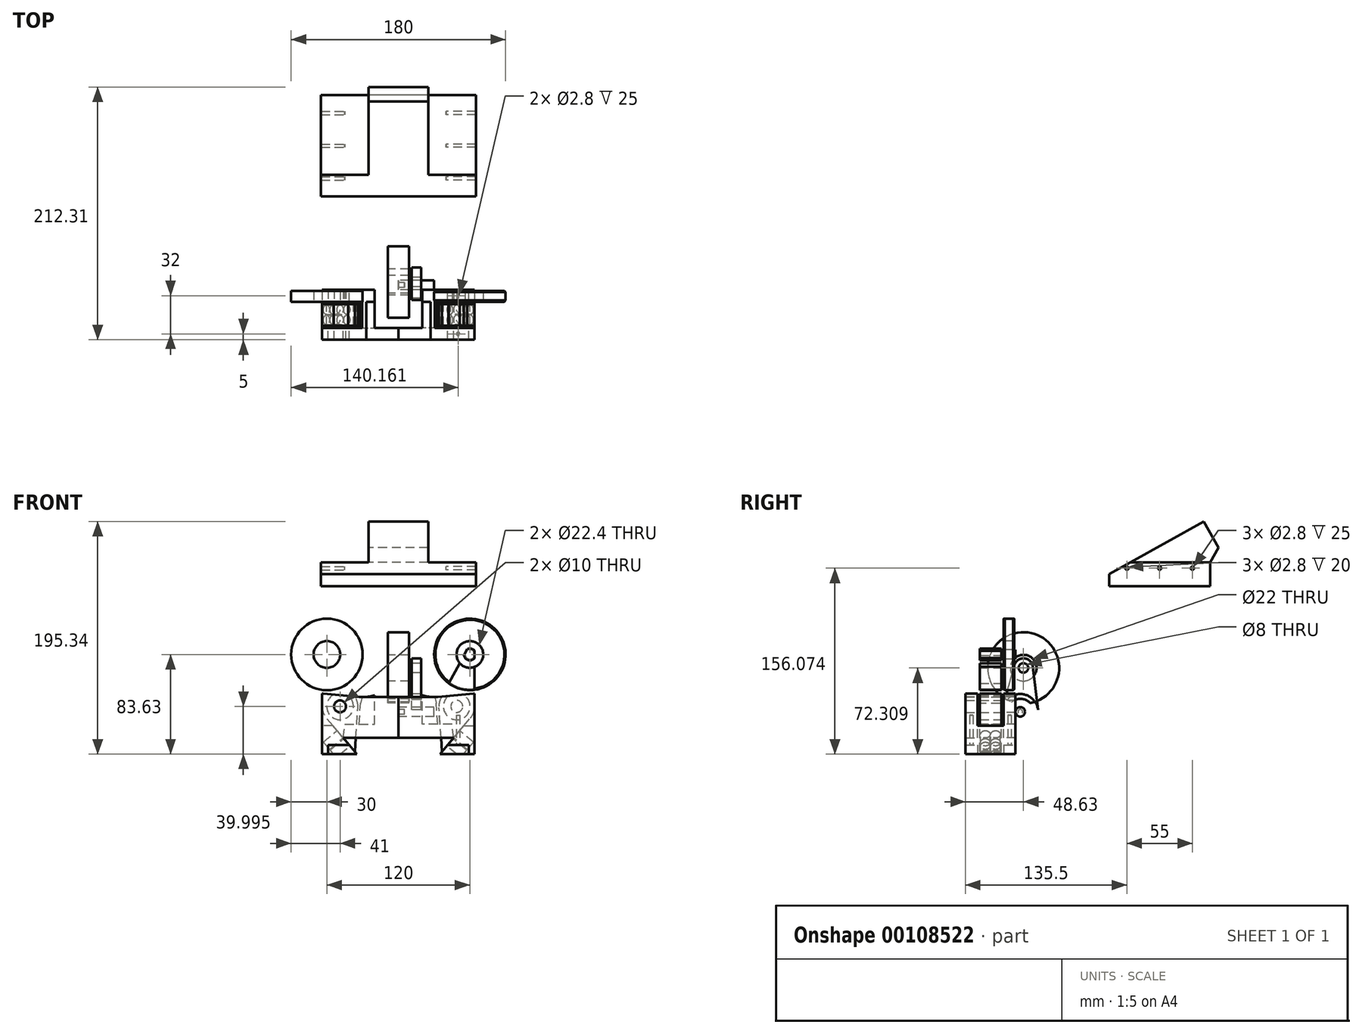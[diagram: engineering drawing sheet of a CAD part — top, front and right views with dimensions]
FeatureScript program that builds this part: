
annotation { "Feature Type Name" : "Feature", "Feature Type Description" : "" }
export const myFeature = defineFeature(function(context is Context, id is Id, definition is map)
    precondition{}
    {
        {
            var Q0;
            Q0=qCreatedBy(makeId("Right.planeOp"),FACE);
            var sketch = newSketch(context, id + "F0", { "sketchPlane" : qUnion([Q0])});
            skLineSegment(sketch, "E0", {"start": v(0, 0) * mm, "end": v(214.16, 119) * mm, "construction": true});
            skPoint(sketch, "E1", {"position": v(196.68, 109.28) * mm});
            skPoint(sketch, "E2", {"position": v(103.39, 57.44) * mm});
            skLineSegment(sketch, "E3", {"start": v(172.6, 107.34) * mm, "end": v(182.3, 89.85) * mm});
            skPoint(sketch, "E4", {"position": v(164.34, 91.3) * mm});
            skLineSegment(sketch, "E5", {"start": v(172.6, 107.34) * mm, "end": v(170.16, 111.7) * mm});
            skLineSegment(sketch, "E6", {"start": v(170.16, 111.7) * mm, "end": v(90.5, 67.44) * mm});
            skLineSegment(sketch, "E7", {"start": v(175.5, 77.44) * mm, "end": v(90.5, 77.44) * mm});
            skLineSegment(sketch, "E8", {"start": v(90.5, 77.44) * mm, "end": v(90.5, 67.44) * mm});
            skLineSegment(sketch, "E9", {"start": v(175.5, 77.44) * mm, "end": v(175.5, 57.44) * mm});
            skLineSegment(sketch, "E10", {"start": v(175.5, 57.44) * mm, "end": v(90.5, 57.44) * mm});
            skLineSegment(sketch, "E11", {"start": v(90.5, 57.44) * mm, "end": v(90.5, 67.44) * mm});
            skLineSegment(sketch, "E12", {"start": v(182.3, 89.85) * mm, "end": v(175.5, 77.44) * mm});
            skSolve(sketch);
        }
        {
            var Q0;
            Q0=qCreatedBy(makeId("Right.planeOp"),FACE);
            var sketch = newSketch(context, id + "F1", { "sketchPlane" : qUnion([Q0])});
            skLineSegment(sketch, "E13", {"start": v(160.5, 72.44) * mm, "end": v(105.5, 72.44) * mm, "construction": true});
            skPoint(sketch, "E14", {"position": v(133, 72.44) * mm});
            skCircle(sketch, "E15", {"center": v(160.5, 72.44) * mm, "radius": 1.4 * mm});
            skCircle(sketch, "E16", {"center": v(133, 72.44) * mm, "radius": 1.4 * mm});
            skCircle(sketch, "E17", {"center": v(105.5, 72.44) * mm, "radius": 1.4 * mm});
            skSolve(sketch);
        }
        {
            var Q0;
            {var subQ0=sQuery(id+"F0.wireOp",EDGE,"E5");Q0=makeQuery(id+"F0.imprint","IMPRINT",FACE,{"disambiguationData":[TD([[makeQuery(id+"F0.imprint","IMPRINT",EDGE,{"derivedFrom":subQ0}),1.0]])]});}
            var Q1;
            {var subQ0=sQuery(id+"F0.wireOp",EDGE,"E9");Q1=makeQuery(id+"F0.imprint","IMPRINT",FACE,{"disambiguationData":[TD([[makeQuery(id+"F0.imprint","IMPRINT",EDGE,{"derivedFrom":subQ0}),-1.0]])]});}
            var Q2;
            {var subQ0=sQuery(id+"F0.wireOp",EDGE,"E12");Q2=makeQuery(id+"F0.imprint","IMPRINT",FACE,{"disambiguationData":[TD([[makeQuery(id+"F0.imprint","IMPRINT",EDGE,{"derivedFrom":subQ0}),-1.0]])]});}
            var Q3;
            {var subQ8=sQuery(id+"F0.wireOp",EDGE,"E11");Q3=makeQuery(id+"F0.imprint","IMPRINT",FACE,{"disambiguationData":[TD([[makeQuery(id+"F0.imprint","IMPRINT",EDGE,{"derivedFrom":subQ8}),-1.0]])]});}
            var Q4;
            {var subQ0=sQuery(id+"F0.wireOp",EDGE,"E10");var subQ1=sQuery(id+"F0.wireOp",EDGE,"sEXiXuxS-OCvZ-XF6I-7GhH-brnsfU8Oz83V");var subQ2=makeQuery(id+"F0.imprint","INTERSECT",VERTEX,{"derivedFrom":[subQ1,subQ0]});Q4=makeQuery(id+"F0.imprint","IMPRINT",FACE,{"disambiguationData":[TD([[makeQuery(id+"F0.imprint","IMPRINT",EDGE,{"disambiguationData":[TD([[subQ2,1.0]])],"derivedFrom":subQ1}),1.0]])]});}
            extrude(context, id + "F2", {"entities" : qUnion([Q0, Q1, Q2, Q3, Q4]), "endBound" : BoundingType.SYMMETRIC, "depth" : 50 * mm});
        }
        {
            var Q0;
            {var subQ0=sQuery(id+"F0.wireOp",EDGE,"E9");Q0=makeQuery(id+"F0.imprint","IMPRINT",FACE,{"disambiguationData":[TD([[makeQuery(id+"F0.imprint","IMPRINT",EDGE,{"derivedFrom":subQ0}),-1.0]])]});}
            var Q1;
            {var subQ0=sQuery(id+"F0.wireOp",EDGE,"OFBeSH8e-VfH7-OQUe-lzTa-2fPhxgrnsW6p");var subQ1=sQuery(id+"F0.wireOp",EDGE,"9e1fb45d-ffff-4d52-95ad-2ab2a11606bd.trimOffspring");var subQ2=makeQuery(id+"F0.imprint","INTERSECT",VERTEX,{"derivedFrom":[subQ1,subQ0]});Q1=makeQuery(id+"F0.imprint","IMPRINT",FACE,{"disambiguationData":[TD([[makeQuery(id+"F0.imprint","IMPRINT",EDGE,{"disambiguationData":[TD([[subQ2,1.0]])],"derivedFrom":subQ1}),-1.0]])]});}
            var Q2;
            {var subQ0=sQuery(id+"F0.wireOp",EDGE,"L8JwAmDp-Vegf-fPRI-g6yE-gIPxQeSgqsUd");var subQ1=sQuery(id+"F0.wireOp",EDGE,"OFBeSH8e-VfH7-OQUe-lzTa-2fPhxgrnsW6p");var subQ2=makeQuery(id+"F0.imprint","INTERSECT",VERTEX,{"derivedFrom":[subQ1,subQ0]});Q2=makeQuery(id+"F0.imprint","IMPRINT",FACE,{"disambiguationData":[TD([[makeQuery(id+"F0.imprint","IMPRINT",EDGE,{"disambiguationData":[TD([[subQ2,-1.0]])],"derivedFrom":subQ1}),-1.0]])]});}
            var Q3;
            {var subQ0=sQuery(id+"F0.wireOp",EDGE,"sEXiXuxS-OCvZ-XF6I-7GhH-brnsfU8Oz83V");var subQ1=sQuery(id+"F0.wireOp",EDGE,"OFBeSH8e-VfH7-OQUe-lzTa-2fPhxgrnsW6p");var subQ2=makeQuery(id+"F0.imprint","INTERSECT",VERTEX,{"derivedFrom":[subQ1,subQ0]});Q3=makeQuery(id+"F0.imprint","IMPRINT",FACE,{"disambiguationData":[TD([[makeQuery(id+"F0.imprint","IMPRINT",EDGE,{"disambiguationData":[TD([[subQ2,-1.0]])],"derivedFrom":subQ1}),-1.0]])]});}
            var Q4;
            {var subQ5=sQuery(id+"F0.wireOp",EDGE,"sEXiXuxS-OCvZ-XF6I-7GhH-brnsfU8Oz83V");var subQ6=sQuery(id+"F0.wireOp",EDGE,"l3UI67aI-0oty-dVZL-KV3C-MkyXoSJzeSSp");var subQ10=makeQuery(id+"F0.imprint","INTERSECT",VERTEX,{"disambiguationData":[OD(0.0)],"derivedFrom":[subQ6,subQ5]});Q4=makeQuery(id+"F0.imprint","IMPRINT",FACE,{"disambiguationData":[TD([[makeQuery(id+"F0.imprint","IMPRINT",EDGE,{"disambiguationData":[TD([[subQ10,1.0]])],"derivedFrom":subQ6}),-1.0]])]});}
            var Q5;
            {var subQ0=sQuery(id+"F0.wireOp",EDGE,"L8JwAmDp-Vegf-fPRI-g6yE-gIPxQeSgqsUd");var subQ1=sQuery(id+"F0.wireOp",EDGE,"l3UI67aI-0oty-dVZL-KV3C-MkyXoSJzeSSp");var subQ9=makeQuery(id+"F0.imprint","INTERSECT",VERTEX,{"disambiguationData":[OD(0.0)],"derivedFrom":[subQ1,subQ0]});Q5=makeQuery(id+"F0.imprint","IMPRINT",FACE,{"disambiguationData":[TD([[makeQuery(id+"F0.imprint","IMPRINT",EDGE,{"disambiguationData":[TD([[subQ9,-1.0]])],"derivedFrom":subQ1}),-1.0]])]});}
            var Q6;
            {var subQ0=sQuery(id+"F0.wireOp",EDGE,"sEXiXuxS-OCvZ-XF6I-7GhH-brnsfU8Oz83V");var subQ1=sQuery(id+"F0.wireOp",EDGE,"l3UI67aI-0oty-dVZL-KV3C-MkyXoSJzeSSp");var subQ2=makeQuery(id+"F0.imprint","INTERSECT",VERTEX,{"disambiguationData":[OD(1.0)],"derivedFrom":[subQ1,subQ0]});Q6=makeQuery(id+"F0.imprint","IMPRINT",FACE,{"disambiguationData":[TD([[makeQuery(id+"F0.imprint","IMPRINT",EDGE,{"disambiguationData":[TD([[subQ2,1.0]])],"derivedFrom":subQ1}),-1.0]])]});}
            var Q7;
            {var subQ0=sQuery(id+"F0.wireOp",EDGE,"sEXiXuxS-OCvZ-XF6I-7GhH-brnsfU8Oz83V");var subQ1=sQuery(id+"F0.wireOp",EDGE,"l3UI67aI-0oty-dVZL-KV3C-MkyXoSJzeSSp");var subQ2=makeQuery(id+"F0.imprint","INTERSECT",VERTEX,{"disambiguationData":[OD(0.0)],"derivedFrom":[subQ1,subQ0]});Q7=makeQuery(id+"F0.imprint","IMPRINT",FACE,{"disambiguationData":[TD([[makeQuery(id+"F0.imprint","IMPRINT",EDGE,{"disambiguationData":[TD([[subQ2,-1.0]])],"derivedFrom":subQ1}),-1.0]])]});}
            var Q8;
            {var subQ0=sQuery(id+"F0.wireOp",EDGE,"E10");var subQ1=sQuery(id+"F0.wireOp",EDGE,"sEXiXuxS-OCvZ-XF6I-7GhH-brnsfU8Oz83V");var subQ2=makeQuery(id+"F0.imprint","INTERSECT",VERTEX,{"derivedFrom":[subQ1,subQ0]});Q8=makeQuery(id+"F0.imprint","IMPRINT",FACE,{"disambiguationData":[TD([[makeQuery(id+"F0.imprint","IMPRINT",EDGE,{"disambiguationData":[TD([[subQ2,1.0]])],"derivedFrom":subQ1}),1.0]])]});}
            var Q9;
            {var subQ8=sQuery(id+"F0.wireOp",EDGE,"E11");Q9=makeQuery(id+"F0.imprint","IMPRINT",FACE,{"disambiguationData":[TD([[makeQuery(id+"F0.imprint","IMPRINT",EDGE,{"derivedFrom":subQ8}),-1.0]])]});}
            extrude(context, id + "F3", {"entities" : qUnion([Q0, Q1, Q2, Q3, Q4, Q5, Q6, Q7, Q8, Q9]), "operationType" : NewBodyOperationType.ADD, "oppositeDirection" : true, "depth" : 65 * mm, "hasSecondDirection" : true, "secondDirectionOppositeDirection" : true, "secondDirectionDepth" : 25 * mm});
        }
        {
            var Q0;
            {var subQ8=sQuery(id+"F0.wireOp",EDGE,"E11");Q0=makeQuery(id+"F0.imprint","IMPRINT",FACE,{"disambiguationData":[TD([[makeQuery(id+"F0.imprint","IMPRINT",EDGE,{"derivedFrom":subQ8}),-1.0]])]});}
            var Q1;
            {var subQ0=sQuery(id+"F0.wireOp",EDGE,"E10");var subQ1=sQuery(id+"F0.wireOp",EDGE,"sEXiXuxS-OCvZ-XF6I-7GhH-brnsfU8Oz83V");var subQ2=makeQuery(id+"F0.imprint","INTERSECT",VERTEX,{"derivedFrom":[subQ1,subQ0]});Q1=makeQuery(id+"F0.imprint","IMPRINT",FACE,{"disambiguationData":[TD([[makeQuery(id+"F0.imprint","IMPRINT",EDGE,{"disambiguationData":[TD([[subQ2,1.0]])],"derivedFrom":subQ1}),1.0]])]});}
            var Q2;
            {var subQ0=sQuery(id+"F0.wireOp",EDGE,"E9");Q2=makeQuery(id+"F0.imprint","IMPRINT",FACE,{"disambiguationData":[TD([[makeQuery(id+"F0.imprint","IMPRINT",EDGE,{"derivedFrom":subQ0}),-1.0]])]});}
            var Q3;
            {var subQ5=sQuery(id+"F0.wireOp",EDGE,"sEXiXuxS-OCvZ-XF6I-7GhH-brnsfU8Oz83V");var subQ6=sQuery(id+"F0.wireOp",EDGE,"l3UI67aI-0oty-dVZL-KV3C-MkyXoSJzeSSp");var subQ10=makeQuery(id+"F0.imprint","INTERSECT",VERTEX,{"disambiguationData":[OD(0.0)],"derivedFrom":[subQ6,subQ5]});Q3=makeQuery(id+"F0.imprint","IMPRINT",FACE,{"disambiguationData":[TD([[makeQuery(id+"F0.imprint","IMPRINT",EDGE,{"disambiguationData":[TD([[subQ10,1.0]])],"derivedFrom":subQ6}),-1.0]])]});}
            var Q4;
            {var subQ0=sQuery(id+"F0.wireOp",EDGE,"L8JwAmDp-Vegf-fPRI-g6yE-gIPxQeSgqsUd");var subQ1=sQuery(id+"F0.wireOp",EDGE,"l3UI67aI-0oty-dVZL-KV3C-MkyXoSJzeSSp");var subQ9=makeQuery(id+"F0.imprint","INTERSECT",VERTEX,{"disambiguationData":[OD(0.0)],"derivedFrom":[subQ1,subQ0]});Q4=makeQuery(id+"F0.imprint","IMPRINT",FACE,{"disambiguationData":[TD([[makeQuery(id+"F0.imprint","IMPRINT",EDGE,{"disambiguationData":[TD([[subQ9,-1.0]])],"derivedFrom":subQ1}),-1.0]])]});}
            var Q5;
            {var subQ0=sQuery(id+"F0.wireOp",EDGE,"sEXiXuxS-OCvZ-XF6I-7GhH-brnsfU8Oz83V");var subQ1=sQuery(id+"F0.wireOp",EDGE,"l3UI67aI-0oty-dVZL-KV3C-MkyXoSJzeSSp");var subQ2=makeQuery(id+"F0.imprint","INTERSECT",VERTEX,{"disambiguationData":[OD(1.0)],"derivedFrom":[subQ1,subQ0]});Q5=makeQuery(id+"F0.imprint","IMPRINT",FACE,{"disambiguationData":[TD([[makeQuery(id+"F0.imprint","IMPRINT",EDGE,{"disambiguationData":[TD([[subQ2,1.0]])],"derivedFrom":subQ1}),-1.0]])]});}
            var Q6;
            {var subQ0=sQuery(id+"F0.wireOp",EDGE,"OFBeSH8e-VfH7-OQUe-lzTa-2fPhxgrnsW6p");var subQ1=sQuery(id+"F0.wireOp",EDGE,"9e1fb45d-ffff-4d52-95ad-2ab2a11606bd.trimOffspring");var subQ2=makeQuery(id+"F0.imprint","INTERSECT",VERTEX,{"derivedFrom":[subQ1,subQ0]});Q6=makeQuery(id+"F0.imprint","IMPRINT",FACE,{"disambiguationData":[TD([[makeQuery(id+"F0.imprint","IMPRINT",EDGE,{"disambiguationData":[TD([[subQ2,1.0]])],"derivedFrom":subQ1}),-1.0]])]});}
            var Q7;
            {var subQ0=sQuery(id+"F0.wireOp",EDGE,"L8JwAmDp-Vegf-fPRI-g6yE-gIPxQeSgqsUd");var subQ1=sQuery(id+"F0.wireOp",EDGE,"OFBeSH8e-VfH7-OQUe-lzTa-2fPhxgrnsW6p");var subQ2=makeQuery(id+"F0.imprint","INTERSECT",VERTEX,{"derivedFrom":[subQ1,subQ0]});Q7=makeQuery(id+"F0.imprint","IMPRINT",FACE,{"disambiguationData":[TD([[makeQuery(id+"F0.imprint","IMPRINT",EDGE,{"disambiguationData":[TD([[subQ2,-1.0]])],"derivedFrom":subQ1}),-1.0]])]});}
            var Q8;
            {var subQ0=sQuery(id+"F0.wireOp",EDGE,"sEXiXuxS-OCvZ-XF6I-7GhH-brnsfU8Oz83V");var subQ1=sQuery(id+"F0.wireOp",EDGE,"OFBeSH8e-VfH7-OQUe-lzTa-2fPhxgrnsW6p");var subQ2=makeQuery(id+"F0.imprint","INTERSECT",VERTEX,{"derivedFrom":[subQ1,subQ0]});Q8=makeQuery(id+"F0.imprint","IMPRINT",FACE,{"disambiguationData":[TD([[makeQuery(id+"F0.imprint","IMPRINT",EDGE,{"disambiguationData":[TD([[subQ2,-1.0]])],"derivedFrom":subQ1}),-1.0]])]});}
            var Q9;
            {var subQ0=sQuery(id+"F0.wireOp",EDGE,"sEXiXuxS-OCvZ-XF6I-7GhH-brnsfU8Oz83V");var subQ1=sQuery(id+"F0.wireOp",EDGE,"l3UI67aI-0oty-dVZL-KV3C-MkyXoSJzeSSp");var subQ2=makeQuery(id+"F0.imprint","INTERSECT",VERTEX,{"disambiguationData":[OD(0.0)],"derivedFrom":[subQ1,subQ0]});Q9=makeQuery(id+"F0.imprint","IMPRINT",FACE,{"disambiguationData":[TD([[makeQuery(id+"F0.imprint","IMPRINT",EDGE,{"disambiguationData":[TD([[subQ2,-1.0]])],"derivedFrom":subQ1}),-1.0]])]});}
            extrude(context, id + "F4", {"entities" : qUnion([Q0, Q1, Q2, Q3, Q4, Q5, Q6, Q7, Q8, Q9]), "operationType" : NewBodyOperationType.ADD, "depth" : 65 * mm, "hasSecondDirection" : true, "secondDirectionOppositeDirection" : false, "secondDirectionDepth" : 25 * mm});
        }
        {
            var Q0;
            Q0=makeQuery(id+"F1.imprint","IMPRINT",FACE,{"disambiguationData":[TD([[makeQuery(id+"F1.imprint","IMPRINT",EDGE,{"derivedFrom":sQuery(id+"F1.wireOp",EDGE,"E17")}),1.0]])]});
            var Q1;
            Q1=makeQuery(id+"F1.imprint","IMPRINT",FACE,{"disambiguationData":[TD([[makeQuery(id+"F1.imprint","IMPRINT",EDGE,{"derivedFrom":sQuery(id+"F1.wireOp",EDGE,"E16")}),1.0]])]});
            var Q2;
            Q2=makeQuery(id+"F1.imprint","IMPRINT",FACE,{"disambiguationData":[TD([[makeQuery(id+"F1.imprint","IMPRINT",EDGE,{"derivedFrom":sQuery(id+"F1.wireOp",EDGE,"E15")}),1.0]])]});
            extrude(context, id + "F5", {"entities" : qUnion([Q0, Q1, Q2]), "operationType" : NewBodyOperationType.REMOVE, "depth" : 65 * mm, "hasSecondDirection" : true, "secondDirectionOppositeDirection" : false, "secondDirectionDepth" : 40 * mm});
        }
        {
            var Q0;
            Q0=makeQuery(id+"F1.imprint","IMPRINT",FACE,{"disambiguationData":[TD([[makeQuery(id+"F1.imprint","IMPRINT",EDGE,{"derivedFrom":sQuery(id+"F1.wireOp",EDGE,"E17")}),1.0]])]});
            var Q1;
            Q1=makeQuery(id+"F1.imprint","IMPRINT",FACE,{"disambiguationData":[TD([[makeQuery(id+"F1.imprint","IMPRINT",EDGE,{"derivedFrom":sQuery(id+"F1.wireOp",EDGE,"E16")}),1.0]])]});
            var Q2;
            Q2=makeQuery(id+"F1.imprint","IMPRINT",FACE,{"disambiguationData":[TD([[makeQuery(id+"F1.imprint","IMPRINT",EDGE,{"derivedFrom":sQuery(id+"F1.wireOp",EDGE,"E15")}),1.0]])]});
            extrude(context, id + "F6", {"entities" : qUnion([Q0, Q1, Q2]), "operationType" : NewBodyOperationType.REMOVE, "oppositeDirection" : true, "depth" : 65 * mm, "hasSecondDirection" : true, "secondDirectionOppositeDirection" : true, "secondDirectionDepth" : 45 * mm});
        }
        {
            var Q0;
            Q0=qCreatedBy(makeId("Front.planeOp"),FACE);
            var sketch = newSketch(context, id + "F7", { "sketchPlane" : qUnion([Q0])});
            skCircle(sketch, "E18", {"center": v(60, 0) * mm, "radius": 4 * mm});
            skCircle(sketch, "E19", {"center": v(60, 0) * mm, "radius": 11.2 * mm});
            skCircle(sketch, "E20", {"center": v(60, 0) * mm, "radius": 30 * mm});
            skPoint(sketch, "E21.middle", {"position": v(0, 0) * mm});
            skCircle(sketch, "E22", {"center": v(49, -43.63) * mm, "radius": 11.2 * mm});
            skCircle(sketch, "E23", {"center": v(49, -43.63) * mm, "radius": 5 * mm});
            skArc(sketch, "E24", {"start": v(35.8, -36.52) * mm, "mid": v(34.34, -40.47) * mm, "end": v(34.04, -44.67) * mm});
            skLineSegment(sketch, "E25", {"start": v(60, 0) * mm, "end": v(49, -43.63) * mm, "construction": true});
            skArc(sketch, "E26", {"start": v(60, 0) * mm, "mid": v(44.75, 1.16) * mm, "end": v(30, -2.84) * mm, "construction": true});
            skCircle(sketch, "E27", {"center": v(30, -2.84) * mm, "radius": 30 * mm, "construction": true});
            skLineSegment(sketch, "E28", {"start": v(64, 0) * mm, "end": v(64, -43.63) * mm});
            skLineSegment(sketch, "E29", {"start": v(60, 0) * mm, "end": v(0, 0) * mm, "construction": true});
            skLineSegment(sketch, "E30", {"start": v(30, -2.84) * mm, "end": v(49, -43.63) * mm, "construction": true});
            skLineSegment(sketch, "E31", {"start": v(49, -43.63) * mm, "end": v(36.6, -81.74) * mm, "construction": true});
            skLineSegment(sketch, "E32", {"start": v(36.6, -81.74) * mm, "end": v(60.5, -53.28) * mm});
            skLineSegment(sketch, "E33", {"start": v(55.05, -59.76) * mm, "end": v(35.02, -83.63) * mm});
            skLineSegment(sketch, "E34", {"start": v(35.02, -83.63) * mm, "end": v(64, -83.63) * mm});
            skLineSegment(sketch, "E35", {"start": v(55.05, -59.76) * mm, "end": v(64, -83.63) * mm});
            skLineSegment(sketch, "E36", {"start": v(64, -43.63) * mm, "end": v(64, -83.63) * mm});
            skLineSegment(sketch, "E37", {"start": v(64, -83.63) * mm, "end": v(49, -43.63) * mm});
            skArc(sketch, "E38", {"start": v(64, -32.76) * mm, "mid": v(63.56, -32.8) * mm, "end": v(63.11, -32.85) * mm});
            skArc(sketch, "E39", {"start": v(0, -16.6) * mm, "mid": v(13.5, -31.43) * mm, "end": v(33.11, -35.7) * mm});
            skLineSegment(sketch, "E40", {"start": v(33.11, -35.7) * mm, "end": v(63.11, -32.85) * mm});
            skLineSegment(sketch, "E41", {"start": v(0, -16.6) * mm, "end": v(0, -48.63) * mm});
            skLineSegment(sketch, "E42", {"start": v(0, -48.63) * mm, "end": v(49, -48.63) * mm});
            skLineSegment(sketch, "E43", {"start": v(49, -58.63) * mm, "end": v(54.63, -58.63) * mm});
            skLineSegment(sketch, "E44", {"start": v(49, -58.63) * mm, "end": v(0, -58.63) * mm});
            skLineSegment(sketch, "E45", {"start": v(0, -58.63) * mm, "end": v(0, -48.63) * mm});
            skLineSegment(sketch, "E46", {"start": v(36.6, -81.74) * mm, "end": v(34.04, -44.67) * mm});
            skCircle(sketch, "E47", {"center": v(30, -2.84) * mm, "radius": 5 * mm, "construction": true});
            skLineSegment(sketch, "E48", {"start": v(33.95, 0.22) * mm, "end": v(59.86, -33.16) * mm, "construction": true});
            skLineSegment(sketch, "E49", {"start": v(30.58, -35.84) * mm, "end": v(31.76, -40.74) * mm});
            skLineSegment(sketch, "E50", {"start": v(33, -58.63) * mm, "end": v(31.76, -40.74) * mm});
            skLineSegment(sketch, "E51", {"start": v(58.94, -70.14) * mm, "end": v(46.34, -70.14) * mm});
            skLineSegment(sketch, "E52", {"start": v(46.34, -70.14) * mm, "end": v(45, -58.63) * mm});
            skArc(sketch, "E53.trimOffspring", {"start": v(60.5, -53.28) * mm, "mid": v(63.1, -48.77) * mm, "end": v(64, -43.63) * mm});
            skLineSegment(sketch, "E54", {"start": v(55.05, -59.76) * mm, "end": v(64, -59.76) * mm});
            skLineSegment(sketch, "E55", {"start": v(58.94, -70.14) * mm, "end": v(58.94, -83.63) * mm});
            skLineSegment(sketch, "E56", {"start": v(58.94, -76.05) * mm, "end": v(41.38, -76.05) * mm});
            skLineSegment(sketch, "E57", {"start": v(64, 0) * mm, "end": v(64, 3) * mm});
            skLineSegment(sketch, "E58.trimOffspring", {"start": v(46.14, -17.31) * mm, "end": v(35.8, -36.52) * mm});
            skLineSegment(sketch, "E59", {"start": v(20, -58.63) * mm, "end": v(20, -34.3) * mm});
            skLineSegment(sketch, "E60", {"start": v(46.34, -70.14) * mm, "end": v(0, -70.14) * mm});
            skLineSegment(sketch, "E61", {"start": v(0, -70.14) * mm, "end": v(0, -58.63) * mm});
            skLineSegment(sketch, "E62", {"start": v(33.11, -35.7) * mm, "end": v(0, -35.7) * mm});
            skLineSegment(sketch, "E63", {"start": v(35.8, -36.52) * mm, "end": v(56.48, 1.9) * mm});
            skLineSegment(sketch, "E64", {"start": v(56.48, 1.9) * mm, "end": v(57.9, 4.54) * mm});
            skLineSegment(sketch, "E65.trimOffspring", {"start": v(46.68, -16.18) * mm, "end": v(46.14, -17.31) * mm});
            skArc(sketch, "E66.trimOffspring", {"start": v(55.06, -0.75) * mm, "mid": v(58.78, -4.85) * mm, "end": v(64, -3) * mm});
            skArc(sketch, "E67.trimOffspring", {"start": v(64, 3) * mm, "mid": v(61.22, 4.85) * mm, "end": v(57.9, 4.54) * mm});
            skSolve(sketch);
        }
        {
            var Q0;
            Q0=qCreatedBy(makeId("Right.planeOp"),FACE);
            var sketch = newSketch(context, id + "F8", { "sketchPlane" : qUnion([Q0])});
            skCircle(sketch, "E68", {"center": v(18.63, -11.32) * mm, "radius": 4 * mm});
            skCircle(sketch, "E69", {"center": v(18.63, -11.32) * mm, "radius": 11 * mm});
            skCircle(sketch, "E70", {"center": v(18.63, -11.32) * mm, "radius": 30 * mm});
            skCircle(sketch, "E71", {"center": v(16, -48.23) * mm, "radius": 4 * mm});
            skCircle(sketch, "E72", {"center": v(16, -48.23) * mm, "radius": 15 * mm});
            skCircle(sketch, "E73", {"center": v(16, -48.23) * mm, "radius": 11 * mm});
            skCircle(sketch, "E74", {"center": v(18.63, -11.32) * mm, "radius": 8 * mm});
            skLineSegment(sketch, "E75", {"start": v(30.9, -46.44) * mm, "end": v(26.57, -10.37) * mm});
            skLineSegment(sketch, "E76", {"start": v(1.5, -44.35) * mm, "end": v(10.9, -9.25) * mm});
            skCircle(sketch, "E77", {"center": v(16, -48.23) * mm, "radius": 2 * mm});
            skSolve(sketch);
        }
        {
            var Q0;
            {var subQ0=sQuery(id+"F7.wireOp",EDGE,"RAf1hxB9-9E7Q-r2Wb-QbEJ-y7RWEQAUjdW3");var subQ1=sQuery(id+"F7.wireOp",EDGE,"E19");var subQ2=makeQuery(id+"F7.imprint","INTERSECT",VERTEX,{"derivedFrom":[subQ1,subQ0]});Q0=makeQuery(id+"F7.imprint","IMPRINT",FACE,{"disambiguationData":[TD([[makeQuery(id+"F7.imprint","IMPRINT",EDGE,{"disambiguationData":[TD([[subQ2,1.0]])],"derivedFrom":subQ1}),-1.0]])]});}
            var Q1;
            {var subQ5=sQuery(id+"F7.wireOp",EDGE,"RAf1hxB9-9E7Q-r2Wb-QbEJ-y7RWEQAUjdW3");var subQ8=sQuery(id+"F7.wireOp",EDGE,"E19");var subQ9=makeQuery(id+"F7.imprint","INTERSECT",VERTEX,{"derivedFrom":[subQ8,subQ5]});Q1=makeQuery(id+"F7.imprint","IMPRINT",FACE,{"disambiguationData":[TD([[makeQuery(id+"F7.imprint","IMPRINT",EDGE,{"disambiguationData":[TD([[subQ9,-1.0]])],"derivedFrom":subQ8}),-1.0]])]});}
            var Q2;
            {var subQ0=sQuery(id+"F7.wireOp",EDGE,"E24");var subQ1=sQuery(id+"F7.wireOp",EDGE,"E20");var subQ2=makeQuery(id+"F7.imprint","INTERSECT",VERTEX,{"disambiguationData":[OD(0.0)],"derivedFrom":[subQ1,subQ0]});Q2=makeQuery(id+"F7.imprint","IMPRINT",FACE,{"disambiguationData":[TD([[makeQuery(id+"F7.imprint","IMPRINT",EDGE,{"disambiguationData":[TD([[subQ2,-1.0]])],"derivedFrom":subQ1}),1.0]])]});}
            var Q3;
            {var subQ0=sQuery(id+"F7.wireOp",EDGE,"E22");var subQ1=sQuery(id+"F7.wireOp",EDGE,"E20");var subQ2=makeQuery(id+"F7.imprint","INTERSECT",VERTEX,{"disambiguationData":[OD(0.0)],"derivedFrom":[subQ1,subQ0]});Q3=makeQuery(id+"F7.imprint","IMPRINT",FACE,{"disambiguationData":[TD([[makeQuery(id+"F7.imprint","IMPRINT",EDGE,{"disambiguationData":[TD([[subQ2,-1.0]])],"derivedFrom":subQ1}),1.0]])]});}
            extrude(context, id + "F9", {"entities" : qUnion([Q0, Q1, Q2, Q3]), "oppositeDirection" : true, "depth" : 11 * mm, "hasSecondDirection" : true, "secondDirectionOppositeDirection" : true, "secondDirectionDepth" : 2 * mm});
        }
        {
            var Q0;
            {var subQ0=sQuery(id+"F7.wireOp",EDGE,"E38");Q0=makeQuery(id+"F7.imprint","IMPRINT",FACE,{"disambiguationData":[TD([[makeQuery(id+"F7.imprint","IMPRINT",EDGE,{"derivedFrom":subQ0}),-1.0]])]});}
            var Q1;
            {var subQ3=sQuery(id+"F7.wireOp",EDGE,"E18");Q1=makeQuery(id+"F7.imprint","IMPRINT",FACE,{"disambiguationData":[TD([[makeQuery(id+"F7.imprint","IMPRINT",EDGE,{"derivedFrom":subQ3}),-1.0]])]});}
            var Q2;
            Q2=makeQuery(id+"F7.imprint","IMPRINT",FACE,{"disambiguationData":[TD([[makeQuery(id+"F7.imprint","IMPRINT",EDGE,{"derivedFrom":sQuery(id+"F7.wireOp",EDGE,"E18")}),1.0]])]});
            var Q3;
            {var subQ0=sQuery(id+"F7.wireOp",EDGE,"E38");Q3=makeQuery(id+"F7.imprint","IMPRINT",FACE,{"disambiguationData":[TD([[makeQuery(id+"F7.imprint","IMPRINT",EDGE,{"derivedFrom":subQ0}),-1.0]])]});}
            var Q4;
            {var subQ0=sQuery(id+"F7.wireOp",EDGE,"E43");Q4=makeQuery(id+"F7.imprint","IMPRINT",FACE,{"disambiguationData":[TD([[makeQuery(id+"F7.imprint","IMPRINT",EDGE,{"derivedFrom":subQ0}),1.0]])]});}
            var Q5;
            {var subQ0=sQuery(id+"F7.wireOp",EDGE,"E43");Q5=makeQuery(id+"F7.imprint","IMPRINT",FACE,{"disambiguationData":[TD([[makeQuery(id+"F7.imprint","IMPRINT",EDGE,{"derivedFrom":subQ0}),-1.0]])]});}
            var Q6;
            {var subQ0=sQuery(id+"F7.wireOp",EDGE,"E43");Q6=makeQuery(id+"F7.imprint","IMPRINT",FACE,{"disambiguationData":[TD([[makeQuery(id+"F7.imprint","IMPRINT",EDGE,{"derivedFrom":subQ0}),1.0]])]});}
            var Q7;
            {var subQ9=sQuery(id+"F7.wireOp",EDGE,"E24");Q7=makeQuery(id+"F7.imprint","IMPRINT",FACE,{"disambiguationData":[TD([[makeQuery(id+"F7.imprint","IMPRINT",EDGE,{"derivedFrom":subQ9}),1.0]])]});}
            var Q8;
            {var subQ1=sQuery(id+"F7.wireOp",EDGE,"E32");Q8=makeQuery(id+"F7.imprint","IMPRINT",FACE,{"disambiguationData":[TD([[makeQuery(id+"F7.imprint","IMPRINT",EDGE,{"derivedFrom":subQ1}),1.0]])]});}
            var Q9;
            {var subQ0=sQuery(id+"F7.wireOp",EDGE,"E28");var subQ3=sQuery(id+"F7.wireOp",EDGE,"E19");var subQ4=makeQuery(id+"F7.imprint","INTERSECT",VERTEX,{"derivedFrom":[subQ3,subQ0]});Q9=makeQuery(id+"F7.imprint","IMPRINT",FACE,{"disambiguationData":[TD([[makeQuery(id+"F7.imprint","IMPRINT",EDGE,{"disambiguationData":[TD([[subQ4,1.0]])],"derivedFrom":subQ3}),-1.0]])]});}
            var Q10;
            {var subQ0=sQuery(id+"F7.wireOp",EDGE,"E52");Q10=makeQuery(id+"F7.imprint","IMPRINT",FACE,{"disambiguationData":[TD([[makeQuery(id+"F7.imprint","IMPRINT",EDGE,{"derivedFrom":subQ0}),1.0]])]});}
            var Q11;
            {var subQ1=sQuery(id+"F7.wireOp",EDGE,"E33");var subQ4=sQuery(id+"F7.wireOp",EDGE,"E46");var subQ6=makeQuery(id+"F7.imprint","INTERSECT",VERTEX,{"derivedFrom":[subQ1,subQ4]});Q11=makeQuery(id+"F7.imprint","IMPRINT",FACE,{"disambiguationData":[TD([[makeQuery(id+"F7.imprint","IMPRINT",EDGE,{"disambiguationData":[TD([[subQ6,1.0]])],"derivedFrom":subQ1}),-1.0]])]});}
            extrude(context, id + "F10", {"entities" : qUnion([Q0, Q1, Q2, Q3, Q4, Q5, Q6, Q7, Q8, Q9, Q10, Q11]), "depth" : 18 * mm});
        }
        {
            var Q0;
            {var subQ0=sQuery(id+"F7.wireOp",EDGE,"E18");var subQ1=makeQuery(id+"F7.imprint","INTERSECT",VERTEX,{"derivedFrom":[subQ0,sQuery(id+"F7.wireOp",EDGE,"RAf1hxB9-9E7Q-r2Wb-QbEJ-y7RWEQAUjdW3")]});Q0=makeQuery(id+"F7.imprint","IMPRINT",FACE,{"disambiguationData":[TD([[makeQuery(id+"F7.imprint","IMPRINT",EDGE,{"disambiguationData":[TD([[subQ1,1.0]])],"derivedFrom":subQ0}),1.0]])]});}
            extrude(context, id + "F11", {"entities" : qUnion([Q0]), "operationType" : NewBodyOperationType.ADD, "oppositeDirection" : true, "depth" : 12 * mm});
        }
        {
            var Q0;
            {var subQ1=sQuery(id+"F7.wireOp",EDGE,"E39");Q0=makeQuery(id+"F7.imprint","IMPRINT",FACE,{"disambiguationData":[TD([[makeQuery(id+"F7.imprint","IMPRINT",EDGE,{"derivedFrom":subQ1}),-1.0]])]});}
            var Q1;
            {var subQ0=sQuery(id+"F7.wireOp",EDGE,"E40");var subQ1=sQuery(id+"F7.wireOp",EDGE,"E22");var subQ2=makeQuery(id+"F7.imprint","INTERSECT",VERTEX,{"disambiguationData":[OD(0.0)],"derivedFrom":[subQ1,subQ0]});Q1=makeQuery(id+"F7.imprint","IMPRINT",FACE,{"disambiguationData":[TD([[makeQuery(id+"F7.imprint","IMPRINT",EDGE,{"disambiguationData":[TD([[subQ2,-1.0]])],"derivedFrom":subQ1}),-1.0]])]});}
            var Q2;
            {var subQ3=sQuery(id+"F7.wireOp",EDGE,"E22");var subQ7=sQuery(id+"F7.wireOp",EDGE,"E40");var subQ9=makeQuery(id+"F7.imprint","INTERSECT",VERTEX,{"disambiguationData":[OD(0.0)],"derivedFrom":[subQ3,subQ7]});Q2=makeQuery(id+"F7.imprint","IMPRINT",FACE,{"disambiguationData":[TD([[makeQuery(id+"F7.imprint","IMPRINT",EDGE,{"disambiguationData":[TD([[subQ9,-1.0]])],"derivedFrom":subQ3}),1.0]])]});}
            var Q3;
            {var subQ3=sQuery(id+"F7.wireOp",EDGE,"E36");Q3=makeQuery(id+"F7.imprint","IMPRINT",FACE,{"disambiguationData":[TD([[makeQuery(id+"F7.imprint","IMPRINT",EDGE,{"derivedFrom":subQ3}),-1.0]])]});}
            var Q4;
            {var subQ3=sQuery(id+"F7.wireOp",EDGE,"E22");var subQ6=sQuery(id+"F7.wireOp",EDGE,"E40");var subQ8=makeQuery(id+"F7.imprint","INTERSECT",VERTEX,{"disambiguationData":[OD(1.0)],"derivedFrom":[subQ3,subQ6]});Q4=makeQuery(id+"F7.imprint","IMPRINT",FACE,{"disambiguationData":[TD([[makeQuery(id+"F7.imprint","IMPRINT",EDGE,{"disambiguationData":[TD([[subQ8,1.0]])],"derivedFrom":subQ3}),-1.0]])]});}
            var Q5;
            {var subQ0=sQuery(id+"F7.wireOp",EDGE,"E44");Q5=makeQuery(id+"F7.imprint","IMPRINT",FACE,{"disambiguationData":[TD([[makeQuery(id+"F7.imprint","IMPRINT",EDGE,{"derivedFrom":subQ0}),-1.0]])]});}
            var Q6;
            {var subQ1=sQuery(id+"F7.wireOp",EDGE,"E22");var subQ6=sQuery(id+"F7.wireOp",EDGE,"E42");var subQ8=makeQuery(id+"F7.imprint","INTERSECT",VERTEX,{"derivedFrom":[subQ1,subQ6]});Q6=makeQuery(id+"F7.imprint","IMPRINT",FACE,{"disambiguationData":[TD([[makeQuery(id+"F7.imprint","IMPRINT",EDGE,{"disambiguationData":[TD([[subQ8,-1.0]])],"derivedFrom":subQ1}),-1.0]])]});}
            var Q7;
            {var subQ0=sQuery(id+"F7.wireOp",EDGE,"E42");var subQ1=sQuery(id+"F7.wireOp",EDGE,"E22");var subQ2=makeQuery(id+"F7.imprint","INTERSECT",VERTEX,{"derivedFrom":[subQ1,subQ0]});Q7=makeQuery(id+"F7.imprint","IMPRINT",FACE,{"disambiguationData":[TD([[makeQuery(id+"F7.imprint","IMPRINT",EDGE,{"disambiguationData":[TD([[subQ2,-1.0]])],"derivedFrom":subQ1}),1.0]])]});}
            var Q8;
            {var subQ5=sQuery(id+"F7.wireOp",EDGE,"E51");Q8=makeQuery(id+"F7.imprint","IMPRINT",FACE,{"disambiguationData":[TD([[makeQuery(id+"F7.imprint","IMPRINT",EDGE,{"derivedFrom":subQ5}),-1.0]])]});}
            var Q9;
            {var subQ1=sQuery(id+"F7.wireOp",EDGE,"E43");Q9=makeQuery(id+"F7.imprint","IMPRINT",FACE,{"disambiguationData":[TD([[makeQuery(id+"F7.imprint","IMPRINT",EDGE,{"derivedFrom":subQ1}),-1.0]])]});}
            var Q10;
            {var subQ0=sQuery(id+"F7.wireOp",EDGE,"E32");var subQ1=sQuery(id+"F7.wireOp",EDGE,"E24");var subQ2=makeQuery(id+"F7.imprint","INTERSECT",VERTEX,{"derivedFrom":[subQ1,subQ0]});Q10=makeQuery(id+"F7.imprint","IMPRINT",FACE,{"disambiguationData":[TD([[makeQuery(id+"F7.imprint","IMPRINT",EDGE,{"disambiguationData":[TD([[subQ2,1.0]])],"derivedFrom":subQ1}),-1.0]])]});}
            var Q11;
            {var subQ0=sQuery(id+"F7.wireOp",EDGE,"E43");Q11=makeQuery(id+"F7.imprint","IMPRINT",FACE,{"disambiguationData":[TD([[makeQuery(id+"F7.imprint","IMPRINT",EDGE,{"derivedFrom":subQ0}),1.0]])]});}
            var Q12;
            {var subQ0=sQuery(id+"F7.wireOp",EDGE,"E50");var subQ1=sQuery(id+"F7.wireOp",EDGE,"E42");var subQ2=makeQuery(id+"F7.imprint","INTERSECT",VERTEX,{"derivedFrom":[subQ1,subQ0]});Q12=makeQuery(id+"F7.imprint","IMPRINT",FACE,{"disambiguationData":[TD([[makeQuery(id+"F7.imprint","IMPRINT",EDGE,{"disambiguationData":[TD([[subQ2,-1.0]])],"derivedFrom":subQ1}),-1.0]])]});}
            var Q13;
            {var subQ3=sQuery(id+"F7.wireOp",EDGE,"E49");Q13=makeQuery(id+"F7.imprint","IMPRINT",FACE,{"disambiguationData":[TD([[makeQuery(id+"F7.imprint","IMPRINT",EDGE,{"derivedFrom":subQ3}),1.0]])]});}
            var Q14;
            {var subQ0=sQuery(id+"F7.wireOp",EDGE,"E46");var subQ1=sQuery(id+"F7.wireOp",EDGE,"E24");var subQ2=makeQuery(id+"F7.imprint","INTERSECT",VERTEX,{"derivedFrom":[subQ1,subQ0]});Q14=makeQuery(id+"F7.imprint","IMPRINT",FACE,{"disambiguationData":[TD([[makeQuery(id+"F7.imprint","IMPRINT",EDGE,{"disambiguationData":[TD([[subQ2,-1.0]])],"derivedFrom":subQ1}),-1.0]])]});}
            var Q15;
            {var subQ5=sQuery(id+"F7.wireOp",EDGE,"E54");Q15=makeQuery(id+"F7.imprint","IMPRINT",FACE,{"disambiguationData":[TD([[makeQuery(id+"F7.imprint","IMPRINT",EDGE,{"derivedFrom":subQ5}),-1.0]])]});}
            var Q16;
            {var subQ1=sQuery(id+"F7.wireOp",EDGE,"E34");var subQ3=sQuery(id+"F7.wireOp",EDGE,"E55");var subQ4=makeQuery(id+"F7.imprint","INTERSECT",VERTEX,{"derivedFrom":[subQ1,subQ3]});Q16=makeQuery(id+"F7.imprint","IMPRINT",FACE,{"disambiguationData":[TD([[makeQuery(id+"F7.imprint","IMPRINT",EDGE,{"disambiguationData":[TD([[subQ4,1.0]])],"derivedFrom":subQ3}),1.0]])]});}
            var Q17;
            {var subQ0=sQuery(id+"F7.wireOp",EDGE,"E59");var subQ1=sQuery(id+"F7.wireOp",EDGE,"E42");var subQ2=makeQuery(id+"F7.imprint","INTERSECT",VERTEX,{"derivedFrom":[subQ1,subQ0]});Q17=makeQuery(id+"F7.imprint","IMPRINT",FACE,{"disambiguationData":[TD([[makeQuery(id+"F7.imprint","IMPRINT",EDGE,{"disambiguationData":[TD([[subQ2,-1.0]])],"derivedFrom":subQ1}),-1.0]])]});}
            var Q18;
            {var subQ0=sQuery(id+"F7.wireOp",EDGE,"E49");Q18=makeQuery(id+"F7.imprint","IMPRINT",FACE,{"disambiguationData":[TD([[makeQuery(id+"F7.imprint","IMPRINT",EDGE,{"derivedFrom":subQ0}),-1.0]])]});}
            extrude(context, id + "F12", {"entities" : qUnion([Q0, Q1, Q2, Q3, Q4, Q5, Q6, Q7, Q8, Q9, Q10, Q11, Q12, Q13, Q14, Q15, Q16, Q17, Q18]), "oppositeDirection" : true, "depth" : 12 * mm, "hasSecondDirection" : true, "secondDirectionOppositeDirection" : true, "secondDirectionDepth" : 2 * mm});
        }
        {
            var Q0;
            {var subQ3=sQuery(id+"F7.wireOp",EDGE,"E22");var subQ7=sQuery(id+"F7.wireOp",EDGE,"E40");var subQ9=makeQuery(id+"F7.imprint","INTERSECT",VERTEX,{"disambiguationData":[OD(0.0)],"derivedFrom":[subQ3,subQ7]});Q0=makeQuery(id+"F7.imprint","IMPRINT",FACE,{"disambiguationData":[TD([[makeQuery(id+"F7.imprint","IMPRINT",EDGE,{"disambiguationData":[TD([[subQ9,-1.0]])],"derivedFrom":subQ3}),1.0]])]});}
            var Q1;
            {var subQ3=sQuery(id+"F7.wireOp",EDGE,"E22");var subQ6=sQuery(id+"F7.wireOp",EDGE,"E40");var subQ8=makeQuery(id+"F7.imprint","INTERSECT",VERTEX,{"disambiguationData":[OD(1.0)],"derivedFrom":[subQ3,subQ6]});Q1=makeQuery(id+"F7.imprint","IMPRINT",FACE,{"disambiguationData":[TD([[makeQuery(id+"F7.imprint","IMPRINT",EDGE,{"disambiguationData":[TD([[subQ8,1.0]])],"derivedFrom":subQ3}),-1.0]])]});}
            var Q2;
            {var subQ0=sQuery(id+"F7.wireOp",EDGE,"E40");var subQ1=sQuery(id+"F7.wireOp",EDGE,"E22");var subQ2=makeQuery(id+"F7.imprint","INTERSECT",VERTEX,{"disambiguationData":[OD(0.0)],"derivedFrom":[subQ1,subQ0]});Q2=makeQuery(id+"F7.imprint","IMPRINT",FACE,{"disambiguationData":[TD([[makeQuery(id+"F7.imprint","IMPRINT",EDGE,{"disambiguationData":[TD([[subQ2,-1.0]])],"derivedFrom":subQ1}),-1.0]])]});}
            var Q3;
            {var subQ0=sQuery(id+"F7.wireOp",EDGE,"E44");Q3=makeQuery(id+"F7.imprint","IMPRINT",FACE,{"disambiguationData":[TD([[makeQuery(id+"F7.imprint","IMPRINT",EDGE,{"derivedFrom":subQ0}),-1.0]])]});}
            var Q4;
            {var subQ1=sQuery(id+"F7.wireOp",EDGE,"E22");var subQ6=sQuery(id+"F7.wireOp",EDGE,"E42");var subQ8=makeQuery(id+"F7.imprint","INTERSECT",VERTEX,{"derivedFrom":[subQ1,subQ6]});Q4=makeQuery(id+"F7.imprint","IMPRINT",FACE,{"disambiguationData":[TD([[makeQuery(id+"F7.imprint","IMPRINT",EDGE,{"disambiguationData":[TD([[subQ8,-1.0]])],"derivedFrom":subQ1}),-1.0]])]});}
            var Q5;
            {var subQ0=sQuery(id+"F7.wireOp",EDGE,"E42");var subQ1=sQuery(id+"F7.wireOp",EDGE,"E22");var subQ2=makeQuery(id+"F7.imprint","INTERSECT",VERTEX,{"derivedFrom":[subQ1,subQ0]});Q5=makeQuery(id+"F7.imprint","IMPRINT",FACE,{"disambiguationData":[TD([[makeQuery(id+"F7.imprint","IMPRINT",EDGE,{"disambiguationData":[TD([[subQ2,-1.0]])],"derivedFrom":subQ1}),1.0]])]});}
            var Q6;
            {var subQ0=sQuery(id+"F7.wireOp",EDGE,"E50");var subQ1=sQuery(id+"F7.wireOp",EDGE,"E42");var subQ2=makeQuery(id+"F7.imprint","INTERSECT",VERTEX,{"derivedFrom":[subQ1,subQ0]});Q6=makeQuery(id+"F7.imprint","IMPRINT",FACE,{"disambiguationData":[TD([[makeQuery(id+"F7.imprint","IMPRINT",EDGE,{"disambiguationData":[TD([[subQ2,-1.0]])],"derivedFrom":subQ1}),-1.0]])]});}
            var Q7;
            {var subQ3=sQuery(id+"F7.wireOp",EDGE,"E49");Q7=makeQuery(id+"F7.imprint","IMPRINT",FACE,{"disambiguationData":[TD([[makeQuery(id+"F7.imprint","IMPRINT",EDGE,{"derivedFrom":subQ3}),1.0]])]});}
            var Q8;
            {var subQ5=sQuery(id+"F7.wireOp",EDGE,"E54");Q8=makeQuery(id+"F7.imprint","IMPRINT",FACE,{"disambiguationData":[TD([[makeQuery(id+"F7.imprint","IMPRINT",EDGE,{"derivedFrom":subQ5}),-1.0]])]});}
            var Q9;
            {var subQ0=sQuery(id+"F7.wireOp",EDGE,"E53.trimOffspring");Q9=makeQuery(id+"F7.imprint","IMPRINT",FACE,{"disambiguationData":[TD([[makeQuery(id+"F7.imprint","IMPRINT",EDGE,{"derivedFrom":subQ0}),-1.0]])]});}
            var Q10;
            {var subQ3=sQuery(id+"F7.wireOp",EDGE,"E51");Q10=makeQuery(id+"F7.imprint","IMPRINT",FACE,{"disambiguationData":[TD([[makeQuery(id+"F7.imprint","IMPRINT",EDGE,{"derivedFrom":subQ3}),-1.0]])]});}
            var Q11;
            {var subQ0=sQuery(id+"F7.wireOp",EDGE,"E43");Q11=makeQuery(id+"F7.imprint","IMPRINT",FACE,{"disambiguationData":[TD([[makeQuery(id+"F7.imprint","IMPRINT",EDGE,{"derivedFrom":subQ0}),-1.0]])]});}
            var Q12;
            {var subQ1=sQuery(id+"F7.wireOp",EDGE,"E34");var subQ3=sQuery(id+"F7.wireOp",EDGE,"E55");var subQ4=makeQuery(id+"F7.imprint","INTERSECT",VERTEX,{"derivedFrom":[subQ1,subQ3]});Q12=makeQuery(id+"F7.imprint","IMPRINT",FACE,{"disambiguationData":[TD([[makeQuery(id+"F7.imprint","IMPRINT",EDGE,{"disambiguationData":[TD([[subQ4,1.0]])],"derivedFrom":subQ3}),1.0]])]});}
            var Q13;
            {var subQ3=sQuery(id+"F7.wireOp",EDGE,"QAZx4OsE-AyMy-ZIBf-LEii-9zukhr6CEToM");Q13=makeQuery(id+"F7.imprint","IMPRINT",FACE,{"disambiguationData":[TD([[makeQuery(id+"F7.imprint","IMPRINT",EDGE,{"derivedFrom":subQ3}),1.0]])]});}
            var Q14;
            {var subQ0=sQuery(id+"F7.wireOp",EDGE,"E59");var subQ1=sQuery(id+"F7.wireOp",EDGE,"E42");var subQ2=makeQuery(id+"F7.imprint","INTERSECT",VERTEX,{"derivedFrom":[subQ1,subQ0]});Q14=makeQuery(id+"F7.imprint","IMPRINT",FACE,{"disambiguationData":[TD([[makeQuery(id+"F7.imprint","IMPRINT",EDGE,{"disambiguationData":[TD([[subQ2,-1.0]])],"derivedFrom":subQ1}),-1.0]])]});}
            var Q15;
            {var subQ0=sQuery(id+"F7.wireOp",EDGE,"E45");Q15=makeQuery(id+"F7.imprint","IMPRINT",FACE,{"disambiguationData":[TD([[makeQuery(id+"F7.imprint","IMPRINT",EDGE,{"derivedFrom":subQ0}),-1.0]])]});}
            var Q16;
            {var subQ5=sQuery(id+"F7.wireOp",EDGE,"E61");Q16=makeQuery(id+"F7.imprint","IMPRINT",FACE,{"disambiguationData":[TD([[makeQuery(id+"F7.imprint","IMPRINT",EDGE,{"derivedFrom":subQ5}),-1.0]])]});}
            var Q17;
            {var subQ0=sQuery(id+"F7.wireOp",EDGE,"E52");Q17=makeQuery(id+"F7.imprint","IMPRINT",FACE,{"disambiguationData":[TD([[makeQuery(id+"F7.imprint","IMPRINT",EDGE,{"derivedFrom":subQ0}),1.0]])]});}
            var Q18;
            {var subQ0=sQuery(id+"F7.wireOp",EDGE,"E49");Q18=makeQuery(id+"F7.imprint","IMPRINT",FACE,{"disambiguationData":[TD([[makeQuery(id+"F7.imprint","IMPRINT",EDGE,{"derivedFrom":subQ0}),-1.0]])]});}
            var Q19;
            {var subQ0=sQuery(id+"F7.wireOp",EDGE,"E42");var subQ5=sQuery(id+"F7.wireOp",EDGE,"E59");var subQ6=makeQuery(id+"F7.imprint","INTERSECT",VERTEX,{"derivedFrom":[subQ0,subQ5]});Q19=makeQuery(id+"F7.imprint","IMPRINT",FACE,{"disambiguationData":[TD([[makeQuery(id+"F7.imprint","IMPRINT",EDGE,{"disambiguationData":[TD([[subQ6,-1.0]])],"derivedFrom":subQ5}),1.0]])]});}
            extrude(context, id + "F13", {"entities" : qUnion([Q0, Q1, Q2, Q3, Q4, Q5, Q6, Q7, Q8, Q9, Q10, Q11, Q12, Q13, Q14, Q15, Q16, Q17, Q18, Q19]), "depth" : 30 * mm, "hasSecondDirection" : true, "secondDirectionOppositeDirection" : false, "secondDirectionDepth" : 20 * mm});
        }
        {
            var Q0;
            {var subQ0=sQuery(id+"F7.wireOp",EDGE,"E49");Q0=makeQuery(id+"F7.imprint","IMPRINT",FACE,{"disambiguationData":[TD([[makeQuery(id+"F7.imprint","IMPRINT",EDGE,{"derivedFrom":subQ0}),-1.0]])]});}
            var Q1;
            {var subQ0=sQuery(id+"F7.wireOp",EDGE,"E59");var subQ1=sQuery(id+"F7.wireOp",EDGE,"E42");var subQ2=makeQuery(id+"F7.imprint","INTERSECT",VERTEX,{"derivedFrom":[subQ1,subQ0]});Q1=makeQuery(id+"F7.imprint","IMPRINT",FACE,{"disambiguationData":[TD([[makeQuery(id+"F7.imprint","IMPRINT",EDGE,{"disambiguationData":[TD([[subQ2,-1.0]])],"derivedFrom":subQ1}),-1.0]])]});}
            extrude(context, id + "F14", {"entities" : qUnion([Q0, Q1]), "operationType" : NewBodyOperationType.ADD, "depth" : 20 * mm, "hasSecondDirection" : true, "secondDirectionOppositeDirection" : true, "secondDirectionDepth" : 2 * mm});
        }
        {
            var Q0;
            {var subQ0=sQuery(id+"F7.wireOp",EDGE,"E51");Q0=makeQuery(id+"F7.imprint","IMPRINT",FACE,{"disambiguationData":[TD([[makeQuery(id+"F7.imprint","IMPRINT",EDGE,{"derivedFrom":subQ0}),1.0]])]});}
            extrude(context, id + "F15", {"entities" : qUnion([Q0]), "depth" : 30 * mm, "hasSecondDirection" : true, "secondDirectionOppositeDirection" : true, "secondDirectionDepth" : 12 * mm});
        }
        {
            var Q0;
            {var subQ3=sQuery(id+"F7.wireOp",EDGE,"E51");Q0=makeQuery(id+"F7.imprint","IMPRINT",FACE,{"disambiguationData":[TD([[makeQuery(id+"F7.imprint","IMPRINT",EDGE,{"derivedFrom":subQ3}),-1.0]])]});}
            var Q1;
            {var subQ5=sQuery(id+"F7.wireOp",EDGE,"E54");Q1=makeQuery(id+"F7.imprint","IMPRINT",FACE,{"disambiguationData":[TD([[makeQuery(id+"F7.imprint","IMPRINT",EDGE,{"derivedFrom":subQ5}),-1.0]])]});}
            var Q2;
            {var subQ3=sQuery(id+"F7.wireOp",EDGE,"l9bVwOZa-TtGl-lHnc-fkOz-mVb4UaNAZxaZ");Q2=makeQuery(id+"F7.imprint","IMPRINT",FACE,{"disambiguationData":[TD([[makeQuery(id+"F7.imprint","IMPRINT",EDGE,{"derivedFrom":subQ3}),1.0]])]});}
            var Q3;
            {var subQ1=sQuery(id+"F7.wireOp",EDGE,"E34");var subQ3=sQuery(id+"F7.wireOp",EDGE,"E55");var subQ4=makeQuery(id+"F7.imprint","INTERSECT",VERTEX,{"derivedFrom":[subQ1,subQ3]});Q3=makeQuery(id+"F7.imprint","IMPRINT",FACE,{"disambiguationData":[TD([[makeQuery(id+"F7.imprint","IMPRINT",EDGE,{"disambiguationData":[TD([[subQ4,1.0]])],"derivedFrom":subQ3}),1.0]])]});}
            var Q4;
            {var subQ3=sQuery(id+"F7.wireOp",EDGE,"E56");Q4=makeQuery(id+"F7.imprint","IMPRINT",FACE,{"disambiguationData":[TD([[makeQuery(id+"F7.imprint","IMPRINT",EDGE,{"derivedFrom":subQ3}),1.0]])]});}
            extrude(context, id + "F16", {"entities" : qUnion([Q0, Q1, Q2, Q3, Q4]), "operationType" : NewBodyOperationType.ADD, "depth" : 20 * mm, "hasSecondDirection" : true, "secondDirectionOppositeDirection" : true, "secondDirectionDepth" : 2 * mm});
        }
        {
            var Q0;
            {var subQ0=sQuery(id+"F7.wireOp",EDGE,"E33");Q0=makeQuery(id+"F16.boolean.opBoolean","MERGE",FACE,{"derivedFrom":[makeQuery(id+"F15.opExtrude","SWEPT_FACE",FACE,{"disambiguationData":[OSD([subQ0])]}),makeQuery(id+"F16.opExtrude","SWEPT_FACE",FACE,{"disambiguationData":[OSD([subQ0])]})]});}
            var sketch = newSketch(context, id + "F17", { "sketchPlane" : qUnion([Q0])});
            skLineSegment(sketch, "E78.bottom", {"start": v(13.29, -19.9) * mm, "end": v(4.71, -19.9) * mm, "construction": true});
            skLineSegment(sketch, "E78.top", {"start": v(13.29, -28.7) * mm, "end": v(4.71, -28.7) * mm, "construction": true});
            skLineSegment(sketch, "E78.left", {"start": v(13.29, -19.9) * mm, "end": v(13.29, -28.7) * mm, "construction": true});
            skLineSegment(sketch, "E78.right", {"start": v(4.71, -19.9) * mm, "end": v(4.71, -28.7) * mm, "construction": true});
            skPoint(sketch, "E78.middle", {"position": v(9, -24.3) * mm});
            skCircle(sketch, "E79", {"center": v(13.29, -28.7) * mm, "radius": 4 * mm});
            skCircle(sketch, "E80", {"center": v(13.29, -19.9) * mm, "radius": 4 * mm});
            skCircle(sketch, "E81", {"center": v(4.71, -19.9) * mm, "radius": 4 * mm});
            skCircle(sketch, "E82", {"center": v(4.71, -28.7) * mm, "radius": 4 * mm});
            skPoint(sketch, "E83", {"position": v(9, -41.56) * mm});
            skSolve(sketch);
        }
        {
            var Q0;
            Q0=qSketchRegion(id+"F17",true);
            extrude(context, id + "F18", {"entities" : qUnion([Q0]), "operationType" : NewBodyOperationType.REMOVE, "oppositeDirection" : true, "depth" : 15 * mm});
        }
        {
            var Q0;
            Q0=makeQuery(id+"F13.opExtrude","SWEPT_BODY",BODY,{"disambiguationData":[OSD([sQuery(id+"F7.wireOp",EDGE,"E23"),sQuery(id+"F7.wireOp",EDGE,"E28"),sQuery(id+"F7.wireOp",EDGE,"E34"),sQuery(id+"F7.wireOp",EDGE,"E36"),sQuery(id+"F7.wireOp",EDGE,"E38"),sQuery(id+"F7.wireOp",EDGE,"E39"),sQuery(id+"F7.wireOp",EDGE,"E40"),sQuery(id+"F7.wireOp",EDGE,"E41"),sQuery(id+"F7.wireOp",EDGE,"E44"),sQuery(id+"F7.wireOp",EDGE,"E45"),sQuery(id+"F7.wireOp",EDGE,"E51"),sQuery(id+"F7.wireOp",EDGE,"E52"),sQuery(id+"F7.wireOp",EDGE,"E55")])]});
            var Q1;
            Q1=makeQuery(id+"F10.opExtrude","SWEPT_BODY",BODY,{"disambiguationData":[OSD([sQuery(id+"F7.wireOp",EDGE,"E22"),sQuery(id+"F7.wireOp",EDGE,"E24"),sQuery(id+"F7.wireOp",EDGE,"RAf1hxB9-9E7Q-r2Wb-QbEJ-y7RWEQAUjdW3"),sQuery(id+"F7.wireOp",EDGE,"SPCu45V9-Yj5J-PRiQ-ueF3-aAsRRnwVrxml"),sQuery(id+"F7.wireOp",EDGE,"E28"),sQuery(id+"F7.wireOp",EDGE,"E32"),sQuery(id+"F7.wireOp",EDGE,"E33"),sQuery(id+"F7.wireOp",EDGE,"E46"),sQuery(id+"F7.wireOp",EDGE,"E53.trimOffspring"),sQuery(id+"F7.wireOp",EDGE,"7VZaeeKL-mWGB-P28Y-Nujv-qzCDUf2iWr1t"),sQuery(id+"F7.wireOp",EDGE,"O4uD7KEl-VbJj-IBSY-ku8z-ZAzFgErav0xw")])]});
            var Q2;
            Q2=makeQuery(id+"F12.opExtrude","SWEPT_BODY",BODY,{"disambiguationData":[OSD([sQuery(id+"F7.wireOp",EDGE,"E23"),sQuery(id+"F7.wireOp",EDGE,"E28"),sQuery(id+"F7.wireOp",EDGE,"E34"),sQuery(id+"F7.wireOp",EDGE,"E36"),sQuery(id+"F7.wireOp",EDGE,"E38"),sQuery(id+"F7.wireOp",EDGE,"E39"),sQuery(id+"F7.wireOp",EDGE,"E40"),sQuery(id+"F7.wireOp",EDGE,"E41"),sQuery(id+"F7.wireOp",EDGE,"E44"),sQuery(id+"F7.wireOp",EDGE,"E45"),sQuery(id+"F7.wireOp",EDGE,"E51"),sQuery(id+"F7.wireOp",EDGE,"E52"),sQuery(id+"F7.wireOp",EDGE,"E55")])]});
            var Q3;
            Q3=makeQuery(id+"F14.opExtrude","SWEPT_BODY",BODY,{"disambiguationData":[OSD([sQuery(id+"F7.wireOp",EDGE,"E39"),sQuery(id+"F7.wireOp",EDGE,"E41"),sQuery(id+"F7.wireOp",EDGE,"E44"),sQuery(id+"F7.wireOp",EDGE,"E45"),sQuery(id+"F7.wireOp",EDGE,"E49"),sQuery(id+"F7.wireOp",EDGE,"E50")])]});
            var Q4;
            Q4=makeQuery(id+"F15.opExtrude","SWEPT_BODY",BODY,{"disambiguationData":[OSD([sQuery(id+"F7.wireOp",EDGE,"E33"),sQuery(id+"F7.wireOp",EDGE,"E51"),sQuery(id+"F7.wireOp",EDGE,"E55"),sQuery(id+"F7.wireOp",EDGE,"E56")])]});
            var Q5;
            Q5=makeQuery(id+"F9.opExtrude","SWEPT_BODY",BODY,{"disambiguationData":[OSD([sQuery(id+"F7.wireOp",EDGE,"E19"),sQuery(id+"F7.wireOp",EDGE,"E20")])]});
            var Q6;
            Q6=qCreatedBy(makeId("Right.planeOp"),FACE);
            mirror(context, id + "F19", {"entities" : qUnion([Q0, Q1, Q2, Q3, Q4, Q5]), "mirrorPlane" : qUnion([Q6])});
        }
        {
            var Q0;
            {var subQ1=sQuery(id+"F7.wireOp",EDGE,"E33");var subQ2=sQuery(id+"F7.wireOp",EDGE,"E51");var subQ3=sQuery(id+"F7.wireOp",EDGE,"E56");var subQ4=sQuery(id+"F7.wireOp",EDGE,"E55");Q0=makeQuery(id+"F16.boolean.opBoolean","SPLIT",FACE,{"disambiguationData":[TD([makeQuery(id+"F15.opExtrude","CAP_FACE",FACE,{"disambiguationData":[OSD([subQ1,subQ2,subQ4,subQ3])],"isStart":true})])],"derivedFrom":makeQuery(id+"F15.opExtrude","SWEPT_FACE",FACE,{"disambiguationData":[OSD([subQ3])]})});}
            var sketch = newSketch(context, id + "F20", { "sketchPlane" : qUnion([Q0])});
            skCircle(sketch, "E84", {"center": v(50.16, -7) * mm, "radius": 1.4 * mm});
            skPoint(sketch, "E84.centerSnap0", {"position": v(41.38, -7) * mm});
            skCircle(sketch, "E85", {"center": v(50.16, 25) * mm, "radius": 1.4 * mm});
            skPoint(sketch, "E85.centerSnap0", {"position": v(50.16, -12) * mm});
            skSolve(sketch);
        }
        {
            var Q0;
            Q0=makeQuery(id+"F20.imprint","IMPRINT",FACE,{"disambiguationData":[TD([[makeQuery(id+"F20.imprint","IMPRINT",EDGE,{"derivedFrom":sQuery(id+"F20.wireOp",EDGE,"E84")}),1.0]])]});
            var Q1;
            Q1=makeQuery(id+"F20.imprint","IMPRINT",FACE,{"disambiguationData":[TD([[makeQuery(id+"F20.imprint","IMPRINT",EDGE,{"derivedFrom":sQuery(id+"F20.wireOp",EDGE,"E85")}),1.0]])]});
            extrude(context, id + "F21", {"entities" : qUnion([Q0, Q1]), "operationType" : NewBodyOperationType.REMOVE, "oppositeDirection" : true, "depth" : 25 * mm});
        }
        {
            var Q0;
            {var subQ0=sQuery(id+"F7.wireOp",EDGE,"E23");var subQ1=makeQuery(id+"F7.imprint","INTERSECT",VERTEX,{"derivedFrom":[subQ0,sQuery(id+"F7.wireOp",EDGE,"E42")]});Q0=makeQuery(id+"F7.imprint","IMPRINT",FACE,{"disambiguationData":[TD([[makeQuery(id+"F7.imprint","IMPRINT",EDGE,{"disambiguationData":[TD([[subQ1,-1.0]])],"derivedFrom":subQ0}),1.0]])]});}
            extrude(context, id + "F22", {"entities" : qUnion([Q0]), "operationType" : NewBodyOperationType.ADD, "depth" : 30 * mm, "hasSecondDirection" : true, "secondDirectionOppositeDirection" : true, "secondDirectionDepth" : 12 * mm});
        }
        {
            var Q0;
            {var subQ0=sQuery(id+"F8.wireOp",EDGE,"E75");var subQ1=sQuery(id+"F8.wireOp",EDGE,"E69");var subQ2=makeQuery(id+"F8.imprint","INTERSECT",VERTEX,{"derivedFrom":[subQ1,subQ0]});Q0=makeQuery(id+"F8.imprint","IMPRINT",FACE,{"disambiguationData":[TD([[makeQuery(id+"F8.imprint","IMPRINT",EDGE,{"disambiguationData":[TD([[subQ2,-1.0]])],"derivedFrom":subQ1}),-1.0]])]});}
            var Q1;
            {var subQ0=sQuery(id+"F8.wireOp",EDGE,"E75");var subQ8=sQuery(id+"F8.wireOp",EDGE,"E69");var subQ9=makeQuery(id+"F8.imprint","INTERSECT",VERTEX,{"derivedFrom":[subQ8,subQ0]});Q1=makeQuery(id+"F8.imprint","IMPRINT",FACE,{"disambiguationData":[TD([[makeQuery(id+"F8.imprint","IMPRINT",EDGE,{"disambiguationData":[TD([[subQ9,1.0]])],"derivedFrom":subQ8}),-1.0]])]});}
            var Q2;
            {var subQ0=sQuery(id+"F8.wireOp",EDGE,"E72");var subQ1=sQuery(id+"F8.wireOp",EDGE,"E70");var subQ2=makeQuery(id+"F8.imprint","INTERSECT",VERTEX,{"disambiguationData":[OD(0.0)],"derivedFrom":[subQ1,subQ0]});Q2=makeQuery(id+"F8.imprint","IMPRINT",FACE,{"disambiguationData":[TD([[makeQuery(id+"F8.imprint","IMPRINT",EDGE,{"disambiguationData":[TD([[subQ2,-1.0]])],"derivedFrom":subQ1}),1.0]])]});}
            var Q3;
            {var subQ0=sQuery(id+"F8.wireOp",EDGE,"E73");var subQ1=sQuery(id+"F8.wireOp",EDGE,"E70");var subQ2=makeQuery(id+"F8.imprint","INTERSECT",VERTEX,{"disambiguationData":[OD(0.0)],"derivedFrom":[subQ1,subQ0]});Q3=makeQuery(id+"F8.imprint","IMPRINT",FACE,{"disambiguationData":[TD([[makeQuery(id+"F8.imprint","IMPRINT",EDGE,{"disambiguationData":[TD([[subQ2,-1.0]])],"derivedFrom":subQ1}),1.0]])]});}
            extrude(context, id + "F23", {"entities" : qUnion([Q0, Q1, Q2, Q3]), "endBound" : BoundingType.SYMMETRIC, "depth" : 18 * mm});
        }
        {
            var Q0;
            {var subQ0=sQuery(id+"F8.wireOp",EDGE,"E75");var subQ8=sQuery(id+"F8.wireOp",EDGE,"E69");var subQ9=makeQuery(id+"F8.imprint","INTERSECT",VERTEX,{"derivedFrom":[subQ8,subQ0]});Q0=makeQuery(id+"F8.imprint","IMPRINT",FACE,{"disambiguationData":[TD([[makeQuery(id+"F8.imprint","IMPRINT",EDGE,{"disambiguationData":[TD([[subQ9,1.0]])],"derivedFrom":subQ8}),-1.0]])]});}
            var Q1;
            {var subQ0=sQuery(id+"F8.wireOp",EDGE,"E75");var subQ1=sQuery(id+"F8.wireOp",EDGE,"E69");var subQ2=makeQuery(id+"F8.imprint","INTERSECT",VERTEX,{"derivedFrom":[subQ1,subQ0]});Q1=makeQuery(id+"F8.imprint","IMPRINT",FACE,{"disambiguationData":[TD([[makeQuery(id+"F8.imprint","IMPRINT",EDGE,{"disambiguationData":[TD([[subQ2,1.0]])],"derivedFrom":subQ1}),1.0]])]});}
            var Q2;
            {var subQ0=sQuery(id+"F8.wireOp",EDGE,"E72");var subQ2=sQuery(id+"F8.wireOp",EDGE,"E70");var subQ5=makeQuery(id+"F8.imprint","INTERSECT",VERTEX,{"disambiguationData":[OD(0.0)],"derivedFrom":[subQ2,subQ0]});Q2=makeQuery(id+"F8.imprint","IMPRINT",FACE,{"disambiguationData":[TD([[makeQuery(id+"F8.imprint","IMPRINT",EDGE,{"disambiguationData":[TD([[subQ5,-1.0]])],"derivedFrom":subQ2}),-1.0]])]});}
            var Q3;
            {var subQ0=sQuery(id+"F8.wireOp",EDGE,"E72");var subQ1=sQuery(id+"F8.wireOp",EDGE,"E70");var subQ2=makeQuery(id+"F8.imprint","INTERSECT",VERTEX,{"disambiguationData":[OD(0.0)],"derivedFrom":[subQ1,subQ0]});Q3=makeQuery(id+"F8.imprint","IMPRINT",FACE,{"disambiguationData":[TD([[makeQuery(id+"F8.imprint","IMPRINT",EDGE,{"disambiguationData":[TD([[subQ2,-1.0]])],"derivedFrom":subQ1}),1.0]])]});}
            var Q4;
            Q4=makeQuery(id+"F8.imprint","IMPRINT",FACE,{"disambiguationData":[TD([[makeQuery(id+"F8.imprint","IMPRINT",EDGE,{"derivedFrom":sQuery(id+"F8.wireOp",EDGE,"E68")}),-1.0]])]});
            extrude(context, id + "F24", {"entities" : qUnion([Q0, Q1, Q2, Q3, Q4]), "depth" : 19 * mm, "hasSecondDirection" : true, "secondDirectionOppositeDirection" : false, "secondDirectionDepth" : 11 * mm});
        }
        {
            var Q0;
            Q0=makeQuery(id+"F8.imprint","IMPRINT",FACE,{"disambiguationData":[TD([[makeQuery(id+"F8.imprint","IMPRINT",EDGE,{"derivedFrom":sQuery(id+"F8.wireOp",EDGE,"E71")}),1.0]])]});
            var Q1;
            Q1=makeQuery(id+"F8.imprint","IMPRINT",FACE,{"disambiguationData":[TD([[makeQuery(id+"F8.imprint","IMPRINT",EDGE,{"derivedFrom":sQuery(id+"F8.wireOp",EDGE,"E77")}),1.0]])]});
            extrude(context, id + "F25", {"entities" : qUnion([Q0, Q1]), "operationType" : NewBodyOperationType.ADD, "depth" : 30 * mm});
        }
        {
            var Q0;
            Q0=makeQuery(id+"F8.imprint","IMPRINT",FACE,{"disambiguationData":[TD([[makeQuery(id+"F8.imprint","IMPRINT",EDGE,{"derivedFrom":sQuery(id+"F8.wireOp",EDGE,"E77")}),1.0]])]});
            extrude(context, id + "F26", {"entities" : qUnion([Q0]), "operationType" : NewBodyOperationType.REMOVE, "depth" : 5 * mm});
        }
        {
            var Q0;
            Q0=makeQuery(id+"F9.opExtrude","CAP_EDGE",EDGE,{"disambiguationData":[OSD([sQuery(id+"F7.wireOp",EDGE,"E20")])],"isStart":false});
            var Q1;
            Q1=makeQuery(id+"F9.opExtrude","CAP_EDGE",EDGE,{"disambiguationData":[OSD([sQuery(id+"F7.wireOp",EDGE,"E20")])],"isStart":true});
            chamfer(context, id + "F27", {"entities" : qUnion([Q0, Q1]), "width" : 1 * mm, "tangentPropagation" : true});
        }
    });
